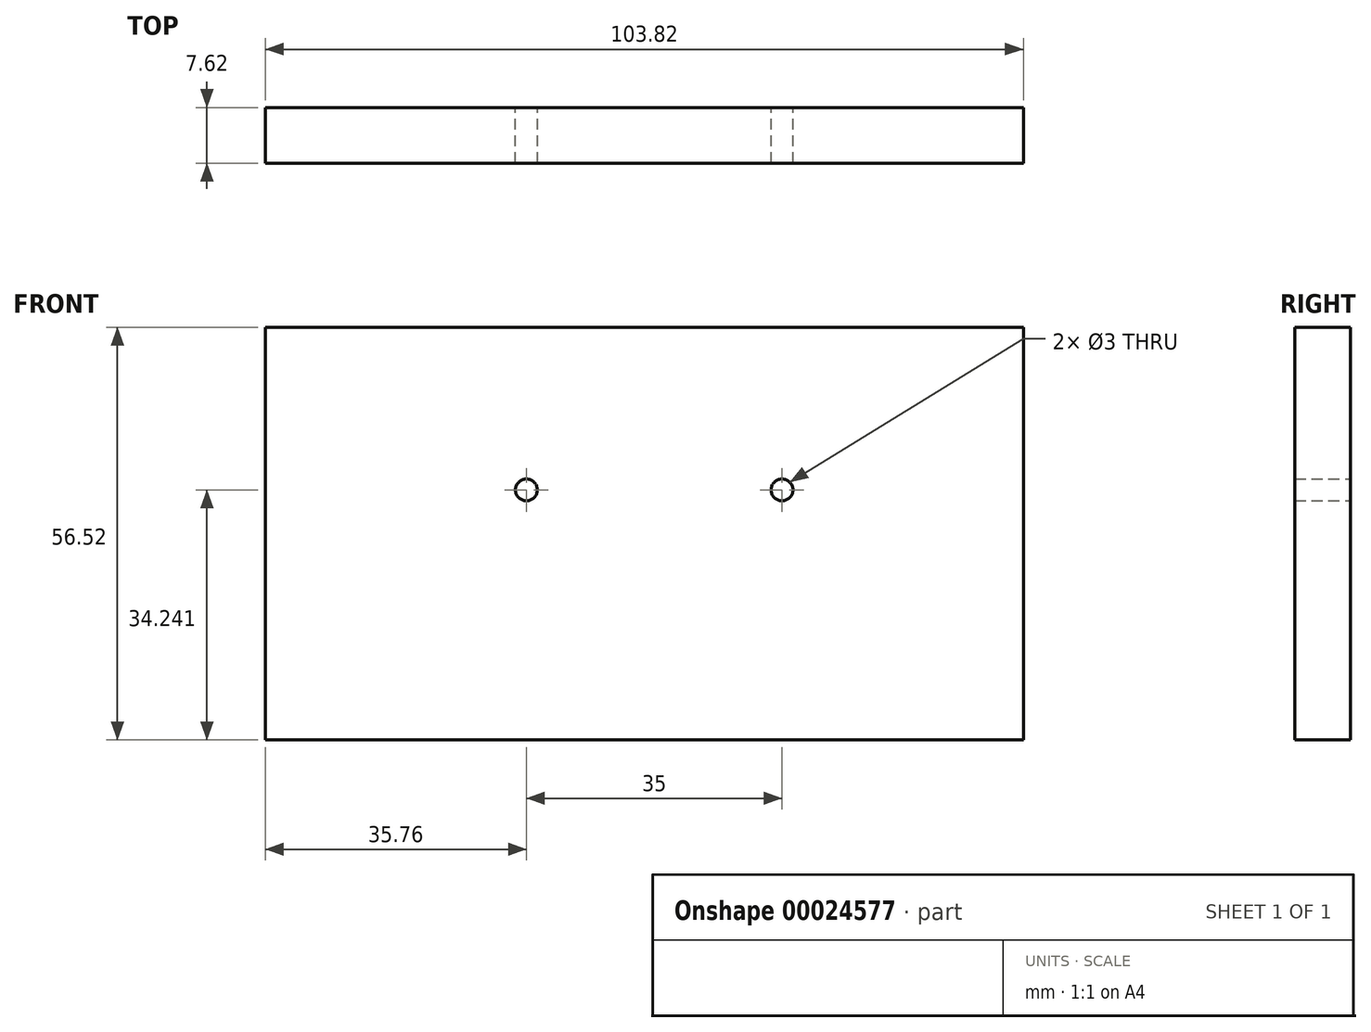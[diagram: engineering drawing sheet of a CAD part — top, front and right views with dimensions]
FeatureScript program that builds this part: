
annotation { "Feature Type Name" : "Feature", "Feature Type Description" : "" }
export const myFeature = defineFeature(function(context is Context, id is Id, definition is map)
    precondition{}
    {
        {
            var Q0;
            Q0=qCreatedBy(makeId("Front.planeOp"),FACE);
            var sketch = newSketch(context, id + "F0", { "sketchPlane" : qUnion([Q0])});
            skLineSegment(sketch, "E0.bottom", {"start": v(-70.76, 16.83) * mm, "end": v(33.06, 16.83) * mm});
            skLineSegment(sketch, "E0.top", {"start": v(-70.76, -39.69) * mm, "end": v(33.06, -39.69) * mm});
            skLineSegment(sketch, "E0.left", {"start": v(-70.76, 16.83) * mm, "end": v(-70.76, -39.69) * mm});
            skLineSegment(sketch, "E0.right", {"start": v(33.06, 16.83) * mm, "end": v(33.06, -39.69) * mm});
            skCircle(sketch, "E1", {"center": v(-35, -5.45) * mm, "radius": 1.5 * mm});
            skCircle(sketch, "E2", {"center": v(0, -5.45) * mm, "radius": 1.5 * mm});
            skLineSegment(sketch, "E3", {"start": v(-35, -5.45) * mm, "end": v(0, -5.45) * mm});
            skLineSegment(sketch, "E4", {"start": v(0, 0) * mm, "end": v(0, -5.45) * mm});
            skSolve(sketch);
        }
        {
            var Q0;
            Q0=makeQuery(id+"F0.imprint","IMPRINT",FACE,{"disambiguationData":[TD([[makeQuery(id+"F0.imprint","IMPRINT",EDGE,{"derivedFrom":sQuery(id+"F0.wireOp",EDGE,"E0.bottom")}),-1.0]])]});
            extrude(context, id + "F1", {"entities" : qUnion([Q0]), "depth" : 7.62 * mm});
        }
    });
